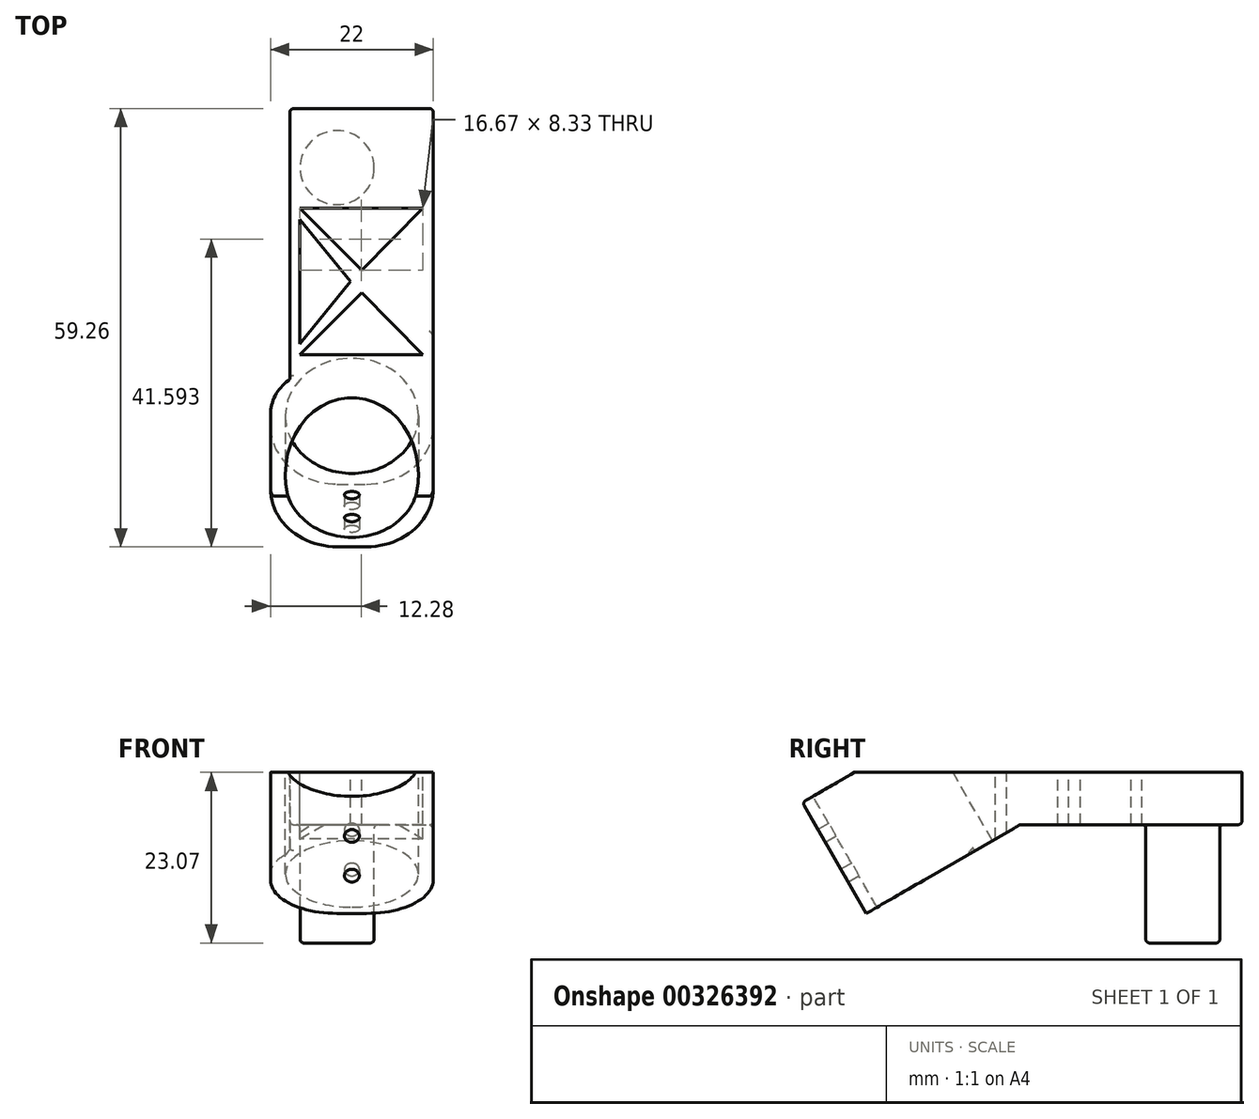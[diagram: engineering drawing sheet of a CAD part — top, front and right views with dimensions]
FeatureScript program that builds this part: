
annotation { "Feature Type Name" : "Feature", "Feature Type Description" : "" }
export const myFeature = defineFeature(function(context is Context, id is Id, definition is map)
    precondition{}
    {
        {
            var Q0;
            Q0=qCreatedBy(makeId("Top.planeOp"),FACE);
            var sketch = newSketch(context, id + "F0", { "sketchPlane" : qUnion([Q0])});
            skCircle(sketch, "E0", {"center": v(0, 0) * mm, "radius": 5 * mm});
            skSolve(sketch);
        }
        {
            var Q0;
            Q0=qSketchRegion(id+"F0",true);
            extrude(context, id + "F1", {"entities" : qUnion([Q0]), "oppositeDirection" : true, "depth" : 16 * mm});
        }
        {
            var Q0;
            Q0=qCreatedBy(makeId("Top.planeOp"),FACE);
            var sketch = newSketch(context, id + "F2", { "sketchPlane" : qUnion([Q0])});
            skCircle(sketch, "E1", {"center": v(0, 0) * mm, "radius": 5 * mm});
            skSolve(sketch);
        }
        {
            var Q0;
            Q0=qCreatedBy(makeId("Top.planeOp"),FACE);
            var sketch = newSketch(context, id + "F3", { "sketchPlane" : qUnion([Q0])});
            skLineSegment(sketch, "E2.bottom", {"start": v(-9, 8) * mm, "end": v(13, 8) * mm});
            skLineSegment(sketch, "E2.top", {"start": v(-9, -22) * mm, "end": v(13, -22) * mm});
            skLineSegment(sketch, "E2.left", {"start": v(-9, 8) * mm, "end": v(-9, -22) * mm});
            skLineSegment(sketch, "E2.right", {"start": v(13, 8) * mm, "end": v(13, -22) * mm});
            skSolve(sketch);
        }
        {
            var Q0;
            Q0=qSketchRegion(id+"F3",true);
            extrude(context, id + "F4", {"entities" : qUnion([Q0]), "operationType" : NewBodyOperationType.ADD, "depth" : 20 * mm});
        }
        {
            var Q0;
            Q0=makeQuery(id+"F4.opExtrude","CAP_EDGE",EDGE,{"disambiguationData":[OSD([sQuery(id+"F3.wireOp",EDGE,"E2.top")])],"isStart":false});
            var Q1;
            Q1=qCreatedBy(makeId("Front.planeOp"),FACE);
            cPlane(context, id + "F5", {"entities" : qUnion([Q0, Q1]), "cplaneType" : CPlaneType.LINE_ANGLE, "offset" : 25 * mm, "angle" : 30 * degree, "width" : 150 * mm, "height" : 150 * mm});
        }
        {
            var Q0;
            Q0=qCreatedBy(id+"F5.planeOp",FACE);
            var sketch = newSketch(context, id + "F6", { "sketchPlane" : qUnion([Q0])});
            skLineSegment(sketch, "E3.bottom", {"start": v(9, 28.32) * mm, "end": v(-13, 28.32) * mm});
            skLineSegment(sketch, "E3.top", {"start": v(9, 11) * mm, "end": v(-13, 11) * mm});
            skLineSegment(sketch, "E3.left", {"start": v(9, 28.32) * mm, "end": v(9, 11) * mm});
            skLineSegment(sketch, "E3.right", {"start": v(-13, 28.32) * mm, "end": v(-13, 11) * mm});
            skSolve(sketch);
        }
        {
            var Q0;
            Q0=qSketchRegion(id+"F6",true);
            extrude(context, id + "F7", {"entities" : qUnion([Q0]), "operationType" : NewBodyOperationType.ADD, "oppositeDirection" : true, "depth" : 34 * mm});
        }
        {
            var Q0;
            Q0=makeQuery(id+"F7.opExtrude","SWEPT_FACE",FACE,{"disambiguationData":[OSD([sQuery(id+"F6.wireOp",EDGE,"E3.bottom")])]});
            cPlane(context, id + "F8", {"entities" : qUnion([Q0]), "cplaneType" : CPlaneType.OFFSET, "offset" : 0 * mm, "width" : 150 * mm, "height" : 150 * mm});
        }
        {
            var Q0;
            Q0=qCreatedBy(id+"F8.planeOp",FACE);
            var sketch = newSketch(context, id + "F9", { "sketchPlane" : qUnion([Q0])});
            skCircle(sketch, "E4", {"center": v(2, -32.38) * mm, "radius": 6 * mm});
            skSolve(sketch);
        }
        {
            var Q0;
            Q0=sQuery(id+"F9.wireOp",VERTEX,"E4.center");
            var Q1;
            Q1=makeQuery(id+"F1.opExtrude","SWEPT_BODY",BODY,{"disambiguationData":[OSD([sQuery(id+"F0.wireOp",EDGE,"E0")])]});
            hole(context, id + "F10", {"style" : HoleStyle.SIMPLE, "endStyle" : HoleEndStyle.THROUGH, "holeDiameter" : 18 * mm, "tappedDepth" : 12 * mm, "tapClearance" : 3, "locations" : qUnion([Q0]), "scope" : qUnion([Q1])});
        }
        {
            var Q0;
            Q0=makeQuery(id+"F7.opExtrude","CAP_FACE",FACE,{"disambiguationData":[OSD([sQuery(id+"F6.wireOp",EDGE,"E3.bottom"),sQuery(id+"F6.wireOp",EDGE,"E3.top"),sQuery(id+"F6.wireOp",EDGE,"E3.left"),sQuery(id+"F6.wireOp",EDGE,"E3.right")])],"isStart":false});
            cPlane(context, id + "F11", {"entities" : qUnion([Q0]), "cplaneType" : CPlaneType.OFFSET, "offset" : 0 * mm, "width" : 150 * mm, "height" : 150 * mm});
        }
        {
            var Q0;
            Q0=qCreatedBy(id+"F11.planeOp",FACE);
            var sketch = newSketch(context, id + "F12", { "sketchPlane" : qUnion([Q0])});
            skCircle(sketch, "E5", {"center": v(2, 16.89) * mm, "radius": 1.5 * mm});
            skCircle(sketch, "E6", {"center": v(2, 23.1) * mm, "radius": 1.1 * mm});
            skSolve(sketch);
        }
        {
            var Q0;
            Q0=sQuery(id+"F12.wireOp",VERTEX,"E5.center");
            var Q1;
            Q1=makeQuery(id+"F1.opExtrude","SWEPT_BODY",BODY,{"disambiguationData":[OSD([sQuery(id+"F0.wireOp",EDGE,"E0")])]});
            hole(context, id + "F13", {"style" : HoleStyle.SIMPLE, "endStyle" : HoleEndStyle.BLIND, "holeDiameter" : 2 * mm, "holeDepth" : 12 * mm, "tappedDepth" : 12 * mm, "tapClearance" : 3, "locations" : qUnion([Q0]), "scope" : qUnion([Q1])});
        }
        {
            var Q0;
            Q0=sQuery(id+"F12.wireOp",VERTEX,"E6.center");
            var Q1;
            Q1=makeQuery(id+"F1.opExtrude","SWEPT_BODY",BODY,{"disambiguationData":[OSD([sQuery(id+"F0.wireOp",EDGE,"E0")])]});
            hole(context, id + "F14", {"style" : HoleStyle.SIMPLE, "endStyle" : HoleEndStyle.BLIND, "holeDiameter" : 2 * mm, "holeDepth" : 12 * mm, "tappedDepth" : 12 * mm, "tapClearance" : 3, "locations" : qUnion([Q0]), "scope" : qUnion([Q1])});
        }
        {
            var Q0;
            Q0=qCreatedBy(makeId("Top.planeOp"),FACE);
            cPlane(context, id + "F15", {"entities" : qUnion([Q0]), "cplaneType" : CPlaneType.OFFSET, "offset" : 13.9 * mm, "width" : 150 * mm, "height" : 150 * mm});
        }
        {
            var Q0;
            Q0=qCreatedBy(id+"F15.planeOp",FACE);
            var sketch = newSketch(context, id + "F16", { "sketchPlane" : qUnion([Q0])});
            skLineSegment(sketch, "E7.bottom", {"start": v(-9, 8) * mm, "end": v(13, 8) * mm});
            skLineSegment(sketch, "E7.top", {"start": v(-9, -32.57) * mm, "end": v(13, -32.57) * mm});
            skLineSegment(sketch, "E7.left", {"start": v(-9, 8) * mm, "end": v(-9, -32.57) * mm});
            skLineSegment(sketch, "E7.right", {"start": v(13, 8) * mm, "end": v(13, -32.57) * mm});
            skSolve(sketch);
        }
        {
            var Q0;
            Q0=qSketchRegion(id+"F16",true);
            extrude(context, id + "F17", {"entities" : qUnion([Q0]), "operationType" : NewBodyOperationType.REMOVE, "depth" : 25 * mm});
        }
        {
            var Q0;
            Q0=makeQuery(id+"F7.opExtrude","CAP_EDGE",EDGE,{"disambiguationData":[OSD([sQuery(id+"F6.wireOp",EDGE,"E3.left")])],"isStart":false});
            fillet(context, id + "F18", {"entities" : qUnion([Q0]), "radius" : 9 * mm, "tangentPropagation" : true, "allowEdgeOverflow" : false});
        }
        {
            var Q0;
            Q0=makeQuery(id+"F7.opExtrude","CAP_EDGE",EDGE,{"disambiguationData":[OSD([sQuery(id+"F6.wireOp",EDGE,"E3.right")])],"isStart":false});
            fillet(context, id + "F19", {"entities" : qUnion([Q0]), "radius" : 9 * mm, "tangentPropagation" : true, "allowEdgeOverflow" : false});
        }
        {
            var Q0;
            Q0=makeQuery(id+"F4.opExtrude","CAP_FACE",FACE,{"disambiguationData":[OSD([sQuery(id+"F3.wireOp",EDGE,"E2.bottom"),sQuery(id+"F3.wireOp",EDGE,"E2.top"),sQuery(id+"F3.wireOp",EDGE,"E2.left"),sQuery(id+"F3.wireOp",EDGE,"E2.right")])],"isStart":true});
            var sketch = newSketch(context, id + "F20", { "sketchPlane" : qUnion([Q0])});
            skLineSegment(sketch, "E8.top", {"start": v(-9, -8) * mm, "end": v(-6.37, -8) * mm});
            skLineSegment(sketch, "E8.left", {"start": v(-9, 33.43) * mm, "end": v(-9, -8) * mm});
            skLineSegment(sketch, "E8.right", {"start": v(-6.37, 28.66) * mm, "end": v(-6.37, -8) * mm});
            skArc(sketch, "E9", {"start": v(-9, 33.43) * mm, "mid": v(-8.3, 30.7) * mm, "end": v(-6.37, 28.66) * mm});
            skSolve(sketch);
        }
        {
            var Q0;
            Q0=qSketchRegion(id+"F20",true);
            extrude(context, id + "F21", {"entities" : qUnion([Q0]), "operationType" : NewBodyOperationType.REMOVE, "endBound" : BoundingType.SYMMETRIC, "oppositeDirection" : true, "depth" : 38 * mm});
        }
        {
            var Q0;
            Q0=makeQuery(id+"F18.opFillet","BLEND_EDGE",EDGE,{"blendedFrom":[makeQuery(id+"F7.opExtrude","CAP_EDGE",EDGE,{"disambiguationData":[OSD([sQuery(id+"F6.wireOp",EDGE,"E3.left")])],"isStart":false}),makeQuery(id+"F7.opExtrude","SWEPT_FACE",FACE,{"disambiguationData":[OSD([sQuery(id+"F6.wireOp",EDGE,"E3.bottom")])]})],"blendedInto":[makeQuery(id+"F7.opExtrude","SWEPT_FACE",FACE,{"disambiguationData":[OSD([sQuery(id+"F6.wireOp",EDGE,"E3.bottom")])]})]});
            var Q1;
            Q1=makeQuery(id+"F10.hole-0.boolean.opBoolean","COPY",EDGE,{"derivedFrom":makeQuery(id+"F10.hole-0.opRevolve","SWEPT_EDGE",EDGE,{"disambiguationData":[OSD([sQuery(id+"F10.hole-0.sketch.wireOp",EDGE,"core_line_2"),sQuery(id+"F10.hole-0.sketch.wireOp",EDGE,"core_line_3")])]})});
            var Q2;
            Q2=makeQuery(id+"F21.boolean.opBoolean","INTERSECT",EDGE,{"derivedFrom":[makeQuery(id+"F17.boolean.opBoolean","COPY",FACE,{"derivedFrom":makeQuery(id+"F17.opExtrude","CAP_FACE",FACE,{"disambiguationData":[OSD([sQuery(id+"F16.wireOp",EDGE,"E7.bottom"),sQuery(id+"F16.wireOp",EDGE,"E7.top"),sQuery(id+"F16.wireOp",EDGE,"E7.left"),sQuery(id+"F16.wireOp",EDGE,"E7.right")])],"isStart":true})}),makeQuery(id+"F21.opExtrude","SWEPT_FACE",FACE,{"disambiguationData":[OSD([sQuery(id+"F20.wireOp",EDGE,"E9")])]})]});
            var Q3;
            Q3=makeQuery(id+"F17.boolean.opBoolean","COPY",FACE,{"derivedFrom":makeQuery(id+"F17.opExtrude","CAP_FACE",FACE,{"disambiguationData":[OSD([sQuery(id+"F16.wireOp",EDGE,"E7.bottom"),sQuery(id+"F16.wireOp",EDGE,"E7.top"),sQuery(id+"F16.wireOp",EDGE,"E7.left"),sQuery(id+"F16.wireOp",EDGE,"E7.right")])],"isStart":true})});
            var Q4;
            Q4=makeQuery(id+"F21.boolean.opBoolean","COPY",FACE,{"derivedFrom":makeQuery(id+"F21.opExtrude","SWEPT_FACE",FACE,{"disambiguationData":[OSD([sQuery(id+"F20.wireOp",EDGE,"E8.right")])]})});
            var Q5;
            Q5=makeQuery(id+"F10.hole-0.boolean.opBoolean","INTERSECT",EDGE,{"derivedFrom":[makeQuery(id+"F7.opExtrude","SWEPT_FACE",FACE,{"disambiguationData":[OSD([sQuery(id+"F6.wireOp",EDGE,"E3.top")])]}),makeQuery(id+"F10.hole-0.opRevolve","SWEPT_FACE",FACE,{"disambiguationData":[OSD([sQuery(id+"F10.hole-0.sketch.wireOp",EDGE,"core_line_2")])]})]});
            var Q6;
            Q6=makeQuery(id+"F4.opExtrude","CAP_FACE",FACE,{"disambiguationData":[OSD([sQuery(id+"F3.wireOp",EDGE,"E2.bottom"),sQuery(id+"F3.wireOp",EDGE,"E2.top"),sQuery(id+"F3.wireOp",EDGE,"E2.left"),sQuery(id+"F3.wireOp",EDGE,"E2.right")])],"isStart":true});
            var Q7;
            Q7=makeQuery(id+"F4.opExtrude","SWEPT_FACE",FACE,{"disambiguationData":[OSD([sQuery(id+"F3.wireOp",EDGE,"E2.bottom")])]});
            var Q8;
            Q8=makeQuery(id+"F1.opExtrude","SWEPT_FACE",FACE,{"disambiguationData":[OSD([sQuery(id+"F0.wireOp",EDGE,"E0")])]});
            fillet(context, id + "F22", {"entities" : qUnion([Q0, Q1, Q2, Q3, Q4, Q5, Q6, Q7, Q8]), "radius" : 0.5 * mm, "tangentPropagation" : true, "allowEdgeOverflow" : false});
        }
        {
            var Q0;
            Q0=makeQuery(id+"F7.boolean.opBoolean","MERGE",FACE,{"derivedFrom":[makeQuery(id+"F4.opExtrude","SWEPT_FACE",FACE,{"disambiguationData":[OSD([sQuery(id+"F3.wireOp",EDGE,"E2.right")])]}),makeQuery(id+"F7.opExtrude","SWEPT_FACE",FACE,{"disambiguationData":[OSD([sQuery(id+"F6.wireOp",EDGE,"E3.right")])]})]});
            var sketch = newSketch(context, id + "F23", { "sketchPlane" : qUnion([Q0])});
            skLineSegment(sketch, "E10.bottom", {"start": v(-47.78, 14.26) * mm, "end": v(13.73, 14.26) * mm});
            skLineSegment(sketch, "E10.top", {"start": v(-47.78, 7.07) * mm, "end": v(13.73, 7.07) * mm});
            skLineSegment(sketch, "E10.left", {"start": v(-47.78, 14.26) * mm, "end": v(-47.78, 7.07) * mm});
            skLineSegment(sketch, "E10.right", {"start": v(13.73, 14.26) * mm, "end": v(13.73, 7.07) * mm});
            skSolve(sketch);
        }
        {
            var Q0;
            Q0 = qSketchRegion(id + "F23", true);
            extrude(context, id + "F24", {"entities" : qUnion([Q0]), "operationType" : NewBodyOperationType.REMOVE, "oppositeDirection" : true, "depth" : 25 * mm});
        }
        {
            var Q0;
            Q0=makeQuery(id+"F24.boolean.opBoolean","COPY",FACE,{"derivedFrom":makeQuery(id+"F24.opExtrude","SWEPT_FACE",FACE,{"disambiguationData":[OSD([sQuery(id+"F23.wireOp",EDGE,"E10.top")])]})});
            var sketch = newSketch(context, id + "F25", { "sketchPlane" : qUnion([Q0])});
            skLineSegment(sketch, "E11", {"start": v(3.31, 8) * mm, "end": v(3.31, -33.3) * mm, "construction": true});
            skLineSegment(sketch, "E12", {"start": v(-11.15, -5.5) * mm, "end": v(16.79, -5.5) * mm, "construction": true});
            skLineSegment(sketch, "E13", {"start": v(-11.15, -15.4) * mm, "end": v(16.79, -15.4) * mm, "construction": true});
            skLineSegment(sketch, "E14", {"start": v(16.59, -25.32) * mm, "end": v(-12.82, -25.32) * mm, "construction": true});
            skLineSegment(sketch, "E15", {"start": v(-5.06, -28.85) * mm, "end": v(-5.06, 0) * mm});
            skLineSegment(sketch, "E16", {"start": v(11.62, -28.78) * mm, "end": v(11.62, 0) * mm});
            skLineSegment(sketch, "E17", {"start": v(-11.42, -16.9) * mm, "end": v(16.94, -16.9) * mm, "construction": true});
            skLineSegment(sketch, "E18.MirrorCS", {"start": v(-11.42, -13.9) * mm, "end": v(16.94, -13.9) * mm, "construction": true});
            skLineSegment(sketch, "E19", {"start": v(-5.06, -25.32) * mm, "end": v(3.31, -16.9) * mm});
            skLineSegment(sketch, "E20", {"start": v(3.31, -16.9) * mm, "end": v(11.62, -25.32) * mm});
            skLineSegment(sketch, "E21", {"start": v(11.62, -25.32) * mm, "end": v(-5.06, -25.32) * mm});
            skLineSegment(sketch, "E22", {"start": v(-5.06, -5.5) * mm, "end": v(3.31, -13.83) * mm});
            skLineSegment(sketch, "E23", {"start": v(3.31, -13.83) * mm, "end": v(11.62, -5.5) * mm});
            skLineSegment(sketch, "E24", {"start": v(11.62, -5.5) * mm, "end": v(-5.06, -5.5) * mm});
            skLineSegment(sketch, "E25", {"start": v(1.81, -29.67) * mm, "end": v(1.81, -1.5) * mm});
            skPoint(sketch, "E25.startSnap0", {"position": v(2, -31.08) * mm});
            skLineSegment(sketch, "E26.MirrorCS", {"start": v(4.81, -29.67) * mm, "end": v(4.81, -1.5) * mm});
            skLineSegment(sketch, "E27", {"start": v(16.78, -7) * mm, "end": v(-7, -7) * mm});
            skLineSegment(sketch, "E28.MirrorCS", {"start": v(16.78, -23.82) * mm, "end": v(-7, -23.82) * mm});
            skLineSegment(sketch, "E29", {"start": v(-5.06, -23.82) * mm, "end": v(1.81, -15.4) * mm});
            skPoint(sketch, "E29.endSnap0", {"position": v(1.81, -15.59) * mm});
            skLineSegment(sketch, "E30", {"start": v(1.81, -15.4) * mm, "end": v(-5.06, -7) * mm});
            skLineSegment(sketch, "E31", {"start": v(-5.06, -7) * mm, "end": v(-5.06, -23.82) * mm});
            skLineSegment(sketch, "E32", {"start": v(11.62, -7) * mm, "end": v(11.62, -23.82) * mm});
            skLineSegment(sketch, "E33", {"start": v(4.81, -15.4) * mm, "end": v(11.62, -7) * mm});
            skLineSegment(sketch, "E34", {"start": v(11.62, -23.82) * mm, "end": v(4.81, -15.4) * mm});
            skSolve(sketch);
        }
        {
            var Q0;
            Q0=makeQuery(id+"F25.imprint","IMPRINT",FACE,{"disambiguationData":[TD([[makeQuery(id+"F25.imprint","IMPRINT",EDGE,{"derivedFrom":sQuery(id+"F25.wireOp",EDGE,"E29")}),1.0]])]});
            var Q1;
            {var subQ0=sQuery(id+"F25.wireOp",EDGE,"E27");var subQ1=sQuery(id+"F25.wireOp",EDGE,"E22");var subQ2=makeQuery(id+"F25.imprint","INTERSECT",VERTEX,{"derivedFrom":[subQ1,subQ0]});Q1=makeQuery(id+"F25.imprint","IMPRINT",FACE,{"disambiguationData":[TD([[makeQuery(id+"F25.imprint","IMPRINT",EDGE,{"disambiguationData":[TD([[subQ2,-1.0]])],"derivedFrom":subQ1}),1.0]])]});}
            var Q2;
            {var subQ0=sQuery(id+"F25.wireOp",EDGE,"E24");var subQ5=sQuery(id+"F25.wireOp",EDGE,"E25");var subQ7=makeQuery(id+"F25.imprint","INTERSECT",VERTEX,{"derivedFrom":[subQ0,subQ5]});Q2=makeQuery(id+"F25.imprint","IMPRINT",FACE,{"disambiguationData":[TD([[makeQuery(id+"F25.imprint","IMPRINT",EDGE,{"disambiguationData":[TD([[subQ7,1.0]])],"derivedFrom":subQ5}),1.0]])]});}
            var Q3;
            {var subQ1=sQuery(id+"F25.wireOp",EDGE,"E23");var subQ6=sQuery(id+"F25.wireOp",EDGE,"E22");var subQ9=makeQuery(id+"F25.imprint","INTERSECT",VERTEX,{"derivedFrom":[subQ6,subQ1]});Q3=makeQuery(id+"F25.imprint","IMPRINT",FACE,{"disambiguationData":[TD([[makeQuery(id+"F25.imprint","IMPRINT",EDGE,{"disambiguationData":[TD([[subQ9,1.0]])],"derivedFrom":subQ6}),1.0]])]});}
            var Q4;
            {var subQ0=sQuery(id+"F25.wireOp",EDGE,"E26.MirrorCS");var subQ1=sQuery(id+"F25.wireOp",EDGE,"E24");var subQ2=makeQuery(id+"F25.imprint","INTERSECT",VERTEX,{"derivedFrom":[subQ1,subQ0]});Q4=makeQuery(id+"F25.imprint","IMPRINT",FACE,{"disambiguationData":[TD([[makeQuery(id+"F25.imprint","IMPRINT",EDGE,{"disambiguationData":[TD([[subQ2,-1.0]])],"derivedFrom":subQ1}),1.0]])]});}
            var Q5;
            {var subQ0=sQuery(id+"F25.wireOp",EDGE,"E24");var subQ5=sQuery(id+"F25.wireOp",EDGE,"E26.MirrorCS");var subQ6=makeQuery(id+"F25.imprint","INTERSECT",VERTEX,{"derivedFrom":[subQ0,subQ5]});Q5=makeQuery(id+"F25.imprint","IMPRINT",FACE,{"disambiguationData":[TD([[makeQuery(id+"F25.imprint","IMPRINT",EDGE,{"disambiguationData":[TD([[subQ6,1.0]])],"derivedFrom":subQ5}),-1.0]])]});}
            var Q6;
            {var subQ0=sQuery(id+"F25.wireOp",EDGE,"E26.MirrorCS");var subQ1=sQuery(id+"F25.wireOp",EDGE,"E23");var subQ2=makeQuery(id+"F25.imprint","INTERSECT",VERTEX,{"derivedFrom":[subQ1,subQ0]});Q6=makeQuery(id+"F25.imprint","IMPRINT",FACE,{"disambiguationData":[TD([[makeQuery(id+"F25.imprint","IMPRINT",EDGE,{"disambiguationData":[TD([[subQ2,-1.0]])],"derivedFrom":subQ1}),1.0]])]});}
            var Q7;
            Q7=makeQuery(id+"F25.imprint","IMPRINT",FACE,{"disambiguationData":[TD([[makeQuery(id+"F25.imprint","IMPRINT",EDGE,{"derivedFrom":sQuery(id+"F25.wireOp",EDGE,"E32")}),-1.0]])]});
            var Q8;
            {var subQ0=sQuery(id+"F25.wireOp",EDGE,"E26.MirrorCS");var subQ1=sQuery(id+"F25.wireOp",EDGE,"E20");var subQ2=makeQuery(id+"F25.imprint","INTERSECT",VERTEX,{"derivedFrom":[subQ1,subQ0]});Q8=makeQuery(id+"F25.imprint","IMPRINT",FACE,{"disambiguationData":[TD([[makeQuery(id+"F25.imprint","IMPRINT",EDGE,{"disambiguationData":[TD([[subQ2,-1.0]])],"derivedFrom":subQ1}),-1.0]])]});}
            var Q9;
            {var subQ1=sQuery(id+"F25.wireOp",EDGE,"E20");var subQ5=sQuery(id+"F25.wireOp",EDGE,"E19");var subQ6=makeQuery(id+"F25.imprint","INTERSECT",VERTEX,{"derivedFrom":[subQ5,subQ1]});Q9=makeQuery(id+"F25.imprint","IMPRINT",FACE,{"disambiguationData":[TD([[makeQuery(id+"F25.imprint","IMPRINT",EDGE,{"disambiguationData":[TD([[subQ6,1.0]])],"derivedFrom":subQ5}),-1.0]])]});}
            var Q10;
            {var subQ0=sQuery(id+"F25.wireOp",EDGE,"E28.MirrorCS");var subQ1=sQuery(id+"F25.wireOp",EDGE,"E19");var subQ2=makeQuery(id+"F25.imprint","INTERSECT",VERTEX,{"derivedFrom":[subQ1,subQ0]});Q10=makeQuery(id+"F25.imprint","IMPRINT",FACE,{"disambiguationData":[TD([[makeQuery(id+"F25.imprint","IMPRINT",EDGE,{"disambiguationData":[TD([[subQ2,-1.0]])],"derivedFrom":subQ1}),-1.0]])]});}
            var Q11;
            {var subQ0=sQuery(id+"F25.wireOp",EDGE,"E21");var subQ5=sQuery(id+"F25.wireOp",EDGE,"E25");var subQ6=makeQuery(id+"F25.imprint","INTERSECT",VERTEX,{"derivedFrom":[subQ0,subQ5]});Q11=makeQuery(id+"F25.imprint","IMPRINT",FACE,{"disambiguationData":[TD([[makeQuery(id+"F25.imprint","IMPRINT",EDGE,{"disambiguationData":[TD([[subQ6,-1.0]])],"derivedFrom":subQ5}),1.0]])]});}
            var Q12;
            {var subQ0=sQuery(id+"F25.wireOp",EDGE,"E26.MirrorCS");var subQ1=sQuery(id+"F25.wireOp",EDGE,"E21");var subQ2=makeQuery(id+"F25.imprint","INTERSECT",VERTEX,{"derivedFrom":[subQ1,subQ0]});Q12=makeQuery(id+"F25.imprint","IMPRINT",FACE,{"disambiguationData":[TD([[makeQuery(id+"F25.imprint","IMPRINT",EDGE,{"disambiguationData":[TD([[subQ2,-1.0]])],"derivedFrom":subQ1}),-1.0]])]});}
            var Q13;
            {var subQ0=sQuery(id+"F25.wireOp",EDGE,"E21");var subQ5=sQuery(id+"F25.wireOp",EDGE,"E26.MirrorCS");var subQ6=makeQuery(id+"F25.imprint","INTERSECT",VERTEX,{"derivedFrom":[subQ0,subQ5]});Q13=makeQuery(id+"F25.imprint","IMPRINT",FACE,{"disambiguationData":[TD([[makeQuery(id+"F25.imprint","IMPRINT",EDGE,{"disambiguationData":[TD([[subQ6,-1.0]])],"derivedFrom":subQ5}),-1.0]])]});}
            extrude(context, id + "F26", {"entities" : qUnion([Q0, Q1, Q2, Q3, Q4, Q5, Q6, Q7, Q8, Q9, Q10, Q11, Q12, Q13]), "operationType" : NewBodyOperationType.REMOVE, "oppositeDirection" : true, "depth" : 25 * mm});
        }
    });
